# Revit family: IS_Melange_A4260_BIM_DE
name_source: partatom
category: Plumbing Fixtures
revit_build: Autodesk Revit 2015 (Build: 20140606_1530(x64)
units: mm (PartAtom-declared; Revit-internal decimal feet)

## types (1)
- A4260AA - MELANGE BSN MXR R-MTD CHROME 1H PUW
    Accessories = www.idealspec.co.uk
    AreaUnits = millimeters
    Assembly Code = C1030200
    AssetType = Fixed
    BIMObjectName = ISI_IdealStandard_WashbasinTaps_Melange_A4260
    BarCode = 4015413316538
    Brand = Ideal Standard
    Color = Chromium Plated
    ConnectionType = Plumbing
    Cost = 0 $
    Description = MELANGE BSN MXR R-MTD CHROME 1H PUW
    DurationUnit = year
    Features = MELANGE BSN MXR R-MTD CHROME 1H PUW
    Finish = Chromium Plated
    Help = www.idealstandard.de
    IfcExportAs = IfcValveType
    IfcExportType = BASIN MIXER
    InstallationInstructions = www.idealstandard.de
    LinearUnits = millimeters
    MainColor = Chromium Plated
    MaintenanceInformation = www.idealstandard.de
    Manufacturer = www.idealstandard.de
    ManufacturerURL = www.idealstandard.de
    Model = A4260AA
    ModelNumber = A4260AA
    ModelReference = MELANGE BSN MXR R-MTD CHROME 1H PUW
    Name = WashbasinTaps_Melange_A4260_ISI
    NettWeight = 2,50 KG
    NominalDepth = 625 mm
    NominalHeight = 116 mm
    NominalLength = 625 mm
    NominalWidth = 250 mm
    ProductInformation = www.idealstandard.de
    Shape = Sculptured
    Size = 116 x 625 x 250 mm
    Space = Internal
    SpareParts = www.idealstandard.de
    TestPressure = 10 bar
    URL = www.idealstandard.de
    Uniclass2015Code = Pr_40_20_87_98
    Uniclass2015Title = Washbasin taps
    Uniclass2015Version = Products v1.1

## geometry (parser evidence)
native form markers: Blend x4
no freeform markers — native parametric forms only
